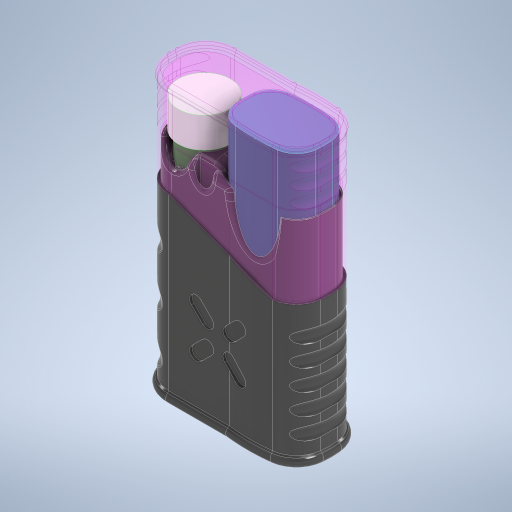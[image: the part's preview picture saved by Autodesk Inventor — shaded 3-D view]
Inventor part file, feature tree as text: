
AUTODESK INVENTOR PART (.ipt)
format: ipt  version: 2024.1 (Build 281209000, 209)  size: 3,479,552 bytes
history: native  units: mm
features: fillet x27, extrude x23, projected_geometry x17, other x6, revolve x5, sketch x5, pattern_circular x2, plane x1, sweep x1, mirror x1
ambient origin geometry x8: Origin, YZ Plane, XZ Plane, XY Plane, X Axis, Y Axis, Z Axis, Center Point
bodies: Body1 (feature_tree), Body2 (feature_tree), Body3 (feature_tree), Body4 (feature_tree)
feature tree (88):
  other  "vape"
  extrude  "Extrusion1"  Depth=8.35mm
  fillet  "Fillet1"  Radius=80.0mm
  extrude  "Extrusion2"  Depth=11.6mm TaperAngle=0.0deg
  plane  "Work Plane1"
  extrude  "Extrusion3"  Depth=45.8mm TaperAngle=0.0deg
  extrude  "Extrusion4"  Depth=22.1mm
  extrude  "Extrusion5"  Depth=1.5mm
  extrude  "Extrusion6"  Depth=1.5mm
  fillet  "Fillet2"  Radius=1.5mm
  extrude  "Extrusion8"  Depth=1.5mm
  extrude  "Extrusion20"  Depth=11.05mm
  extrude  "Extrusion21"  Depth=15.55mm
  sweep  "Sweep2"
  extrude  "Extrusion22"  Depth=3.0mm
  fillet  "Fillet22"  Radius=3.0mm
  fillet  "Fillet23"  Radius=3.0mm
  fillet  "Fillet24"  Radius=11.05mm
  fillet  "Fillet25"  Radius=15.55mm
  fillet  "Fillet26"  Radius=2.0mm
  fillet  "Fillet4"  Radius=13.0mm
  extrude  "Extrusion10"  Depth=12.5mm TaperAngle=0.0deg
  extrude  "Extrusion11"  Depth=2.0mm
  fillet  "Fillet10"  Radius=10.0mm
  fillet  "Fillet27"  Radius=11.0mm
  extrude  "Extrusion13"  Depth=4.0mm
  fillet  "Fillet28"  Radius=2.0mm
  extrude  "Extrusion14"  Depth=3.0mm
  extrude  "Extrusion23"  Depth=72.0mm TaperAngle=0.0deg
  extrude  "Extrusion24"  Depth=2.4mm
  extrude  "Extrusion15"  Depth=7.3mm
  fillet  "Fillet29"  Radius=7.0mm
  extrude  "Extrusion25"  Depth=45.0mm TaperAngle=0.0deg
  fillet  "Fillet30"  Radius=0.25mm
  other  "Work Axis1"
  revolve  "Revolution1"  [1 undecoded]
  sketch  "Sketch30"  dims[d31=17.0mm d38=22.1mm]
  revolve  "Revolution2"  [1 undecoded]
  fillet  "Fillet32"  Radius=3.0mm
  extrude  "Extrusion26"  Depth=1.0mm
  revolve  "Revolution3"  [1 undecoded]
  revolve  "Revolution5"  [1 undecoded]
  extrude  "Extrusion27"  TaperAngle=0.0deg  [1 undecoded]
  extrude  "Extrusion28"  TaperAngle=0.0deg  [1 undecoded]
  fillet  "Fillet34"  Radius=15.0mm
  other  "Work Axis2"
  revolve  "Revolution6"  [1 undecoded]
  pattern_circular  "Circular Pattern1"  Count=2  [1 undecoded]
  extrude  "Extrusion29"  Depth=9.0mm
  fillet  "Fillet35"  Radius=7.5mm
  fillet  "Fillet36"  Radius=6.0mm
  fillet  "Fillet37"  Radius=4.0mm
  fillet  "Fillet38"  Radius=1.0mm
  fillet  "Fillet39"  Radius=2.0mm
  fillet  "Fillet40"  Radius=1.2mm
  fillet  "Fillet41"  Radius=0.5mm
  pattern_circular  "Circular Pattern2"  [2 undecoded]
  fillet  "Fillet42"  Radius=24.0mm
  fillet  "Fillet43"  Radius=2.5mm
  fillet  "Fillet44"  Radius=0.7mm
  fillet  "Fillet45"  Radius=2.35mm
  fillet  "Fillet46"  Radius=4.0mm
  extrude  "Extrusion30"  Depth=0.5mm
  mirror  "Mirror1"
  other  "vape-tube"
  other  "storage"
  projected_geometry  "Projected Loop2"
  projected_geometry  "Projected Loop3"
  projected_geometry  "Projected Loop4"
  projected_geometry  "Projected Loop6"
  other  "vape-lid"
  projected_geometry  "Projected Loop13"
  sketch  "Sketch23"  dims[d4=98.5mm d5=0.0mm d9=8.35mm d22=80.0mm d23=0.0mm]
  projected_geometry  "Projected Loop14"
  sketch  "Sketch25"  dims[d24=20.0mm d26=11.6mm d27=0.0mm]
  projected_geometry  "Projected Loop15"
  projected_geometry  "Projected Loop16"
  projected_geometry  "Projected Loop17"
  projected_geometry  "Projected Loop18"
  projected_geometry  "Projected Loop19"
  projected_geometry  "Projected Loop20"
  sketch  "Sketch29"  dims[d28=17.0mm d29=45.8mm d30=0.0mm]
  projected_geometry  "Projected Loop31"
  sketch  "Sketch37"  dims[d39=31.1mm d41=1.5mm d42=1.5mm d44=1.5mm d45=1.5mm d46=11.05mm d47=15.55mm d48=3.0mm d49=3.0mm d50=3.0mm d51=3.0mm d52=11.05mm d53=15.55mm d54=2.0mm d55=13.0mm d56=12.5mm d57=60.0mm d58=0.0mm d59=2.0mm d60=10.0mm d61=0.0mm d62=11.0mm d66=4.0mm d67=8.726646mm d69=2.0mm d83=3.0mm d86=72.0mm d87=0.0mm d88=2.4mm d89=7.3mm d91=7.0mm d92=45.0mm d93=0.0mm d94=0.25mm d105=71.0mm d106=0.0mm d108=71.0mm d109=0.0mm d110=3.0mm d111=30.0deg d158=1.0mm d159=15.0mm d160=0.0mm d161=15.0mm d162=0.0mm d163=0.0mm d164=0.0mm d169=0.0mm d170=0.0mm d171=15.0mm d172=15.780931mm d173=20.0mm d174=9.0mm d175=7.5mm d176=6.0mm d177=4.0mm d178=1.0mm d179=2.0mm d180=1.2mm d181=0.5mm d182=1.0mm d183=24.0mm d184=2.5mm d185=0.7mm d186=2.35mm d187=4.0mm d188=0.5mm d189=10.0mm d190=0.0mm d191=10.0mm d192=0.0mm d193=1.5mm d194=6.0mm d195=3.65mm d196=10.0mm d197=0.0mm d198=2.5mm d199=14.0mm d200=19.0mm d201=19.0mm d207=180.0deg d208=8.0mm d209=8.0mm d210=8.0mm d211=8.0mm d212=8.0mm d213=12.5mm d215=0.0mm d216=180.0deg d218=1.5mm d220=0.5mm d221=18.25mm d222=0.0mm d223=8.0mm d224=7.0mm d225=6.0mm d226=6.0mm d227=11.5mm d228=6.0mm d229=6.0mm d230=180.0deg d240=3.0mm d241=6.0mm d242=6.0mm d243=6.0mm d244=41.5mm d245=11.5mm d246=6.0mm d247=180.0deg d249=20.0mm d253=22.0mm d254=22.0mm d255=25.0mm d256=1.0mm d257=1.0mm d258=0.0mm d259=1.0mm d260=0.0mm d261=0.2mm d262=11.0mm d263=5.0mm d264=10.0mm d265=2.241222mm d266=10.0mm d267=30.0mm d268=4.0mm d269=45.0deg d270=40.0mm d271=360.0deg d275=0.4mm d276=1.1mm d277=2.4mm d278=3.0mm d279=1.5mm d280=3.0mm d281=0.810487mm d282=2.943591mm d283=4.5mm d284=0.0mm d285=2.0mm d286=0.8mm d287=3.0mm d288=0.5mm d289=1.0mm d290=1.0mm d291=1.0mm d292=40.0mm d293=360.0deg d295=1.0mm d296=0.5mm d297=0.5mm d298=1.0mm d299=0.4mm d309=59.760104mm d310=29.880052mm d311=30.0mm d312=12.0mm d313=45.0deg d315=8.5mm d316=8.5mm d317=5.0mm d318=40.0mm d320=360.0deg d322=10.0mm d323=1.0mm d324=0.0mm d325=0.0mm]
  projected_geometry  "Projected Loop32"
  projected_geometry  "Projected Loop33"
  projected_geometry  "Projected Loop34"
  projected_geometry  "Projected Loop35"
note: 10 required parameter values undecoded (feature->parameter linkage not recoverable at this tier; creation-order binding heuristic only, values carry confidence <= 0.55)